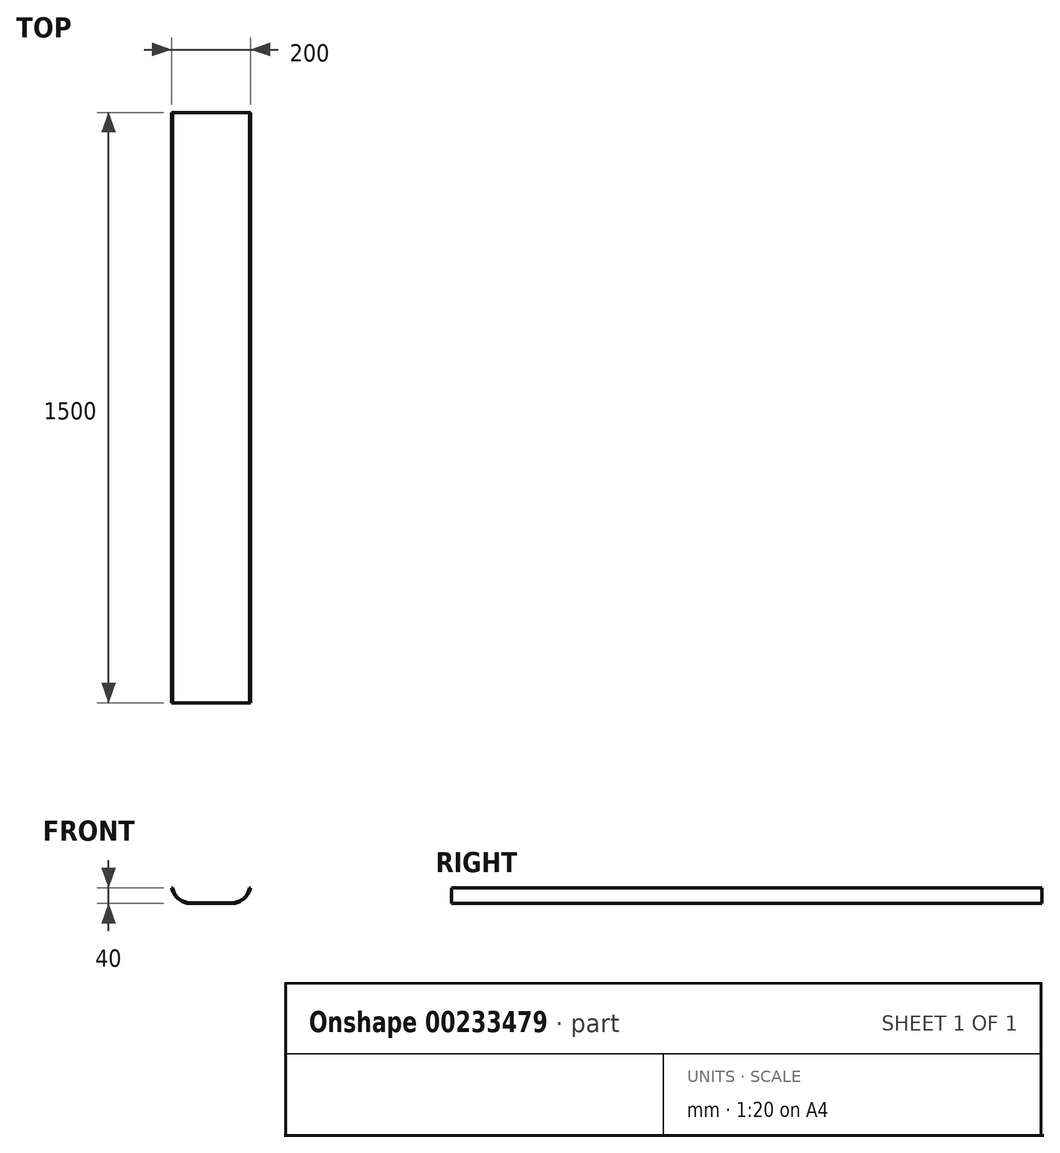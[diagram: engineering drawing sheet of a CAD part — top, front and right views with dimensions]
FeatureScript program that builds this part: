
annotation { "Feature Type Name" : "Feature", "Feature Type Description" : "" }
export const myFeature = defineFeature(function(context is Context, id is Id, definition is map)
    precondition{}
    {
        {
            var Q0;
            Q0=qCreatedBy(makeId("Front.planeOp"),FACE);
            var sketch = newSketch(context, id + "F0", { "sketchPlane" : qUnion([Q0])});
            skLineSegment(sketch, "E0", {"start": v(0, 0) * mm, "end": v(-52.33, 0) * mm});
            skLineSegment(sketch, "E1", {"start": v(-100, 40) * mm, "end": v(-103.8, 61.59) * mm, "construction": true});
            skArc(sketch, "E2", {"start": v(-52.33, 0) * mm, "mid": v(-83.44, 11.32) * mm, "end": v(-100, 40) * mm});
            skLineSegment(sketch, "E3", {"start": v(0, 0) * mm, "end": v(0, 20.65) * mm, "construction": true});
            skArc(sketch, "E4.0", {"start": v(-52.33, 2) * mm, "mid": v(-82.02, 12.74) * mm, "end": v(-97.97, 40) * mm});
            skLineSegment(sketch, "E4.1", {"start": v(0, 2) * mm, "end": v(-52.33, 2) * mm});
            skLineSegment(sketch, "E5", {"start": v(-100, 40) * mm, "end": v(-97.97, 40) * mm});
            skLineSegment(sketch, "E6", {"start": v(0, 2) * mm, "end": v(0, 0) * mm});
            skSolve(sketch);
        }
        {
            var Q0;
            Q0=qSketchRegion(id+"F0",true);
            extrude(context, id + "F1", {"entities" : qUnion([Q0]), "depth" : 1500 * mm});
        }
        {
            var Q0;
            Q0=makeQuery(id+"F1.opExtrude","SWEPT_BODY",BODY,{"disambiguationData":[OSD([sQuery(id+"F0.wireOp",EDGE,"E0"),sQuery(id+"F0.wireOp",EDGE,"E2"),sQuery(id+"F0.wireOp",EDGE,"E4.0"),sQuery(id+"F0.wireOp",EDGE,"E4.1"),sQuery(id+"F0.wireOp",EDGE,"E5"),sQuery(id+"F0.wireOp",EDGE,"E6")])]});
            var Q1;
            Q1=qCreatedBy(makeId("Right.planeOp"),FACE);
            mirror(context, id + "F2", {"operationType" : NewBodyOperationType.ADD, "entities" : qUnion([Q0]), "mirrorPlane" : qUnion([Q1])});
        }
    });
